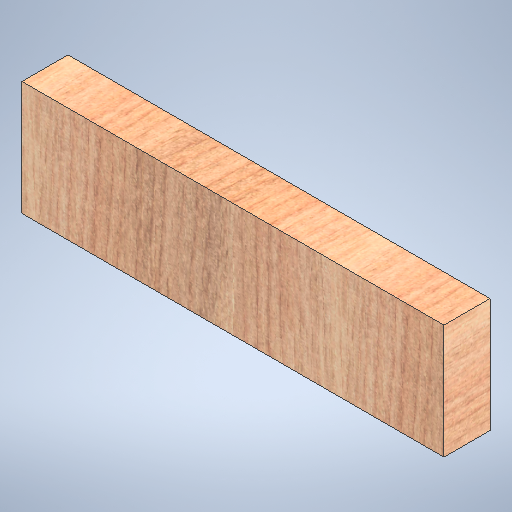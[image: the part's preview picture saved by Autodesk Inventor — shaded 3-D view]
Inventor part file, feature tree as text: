
AUTODESK INVENTOR PART (.ipt)
format: ipt  version: 2025 (Build 290162010, 162A)  size: 474,112 bytes
history: native  units: in
note: dims shown in document units (in); Inventor stores cm internally (conversion verified against a paired STEP export)
features: extrude x1, sketch x1
ambient origin geometry x8: Origin, YZ Plane, XZ Plane, XY Plane, X Axis, Y Axis, Z Axis, Center Point
bodies: Solid1 (feature_tree)
feature tree (2):
  extrude  "Extrusion1"  Depth=13.75in
  sketch  "Sketch1"  dims[d2=3.725in d3=13.75in d4=1.5in d5=0.0in]
